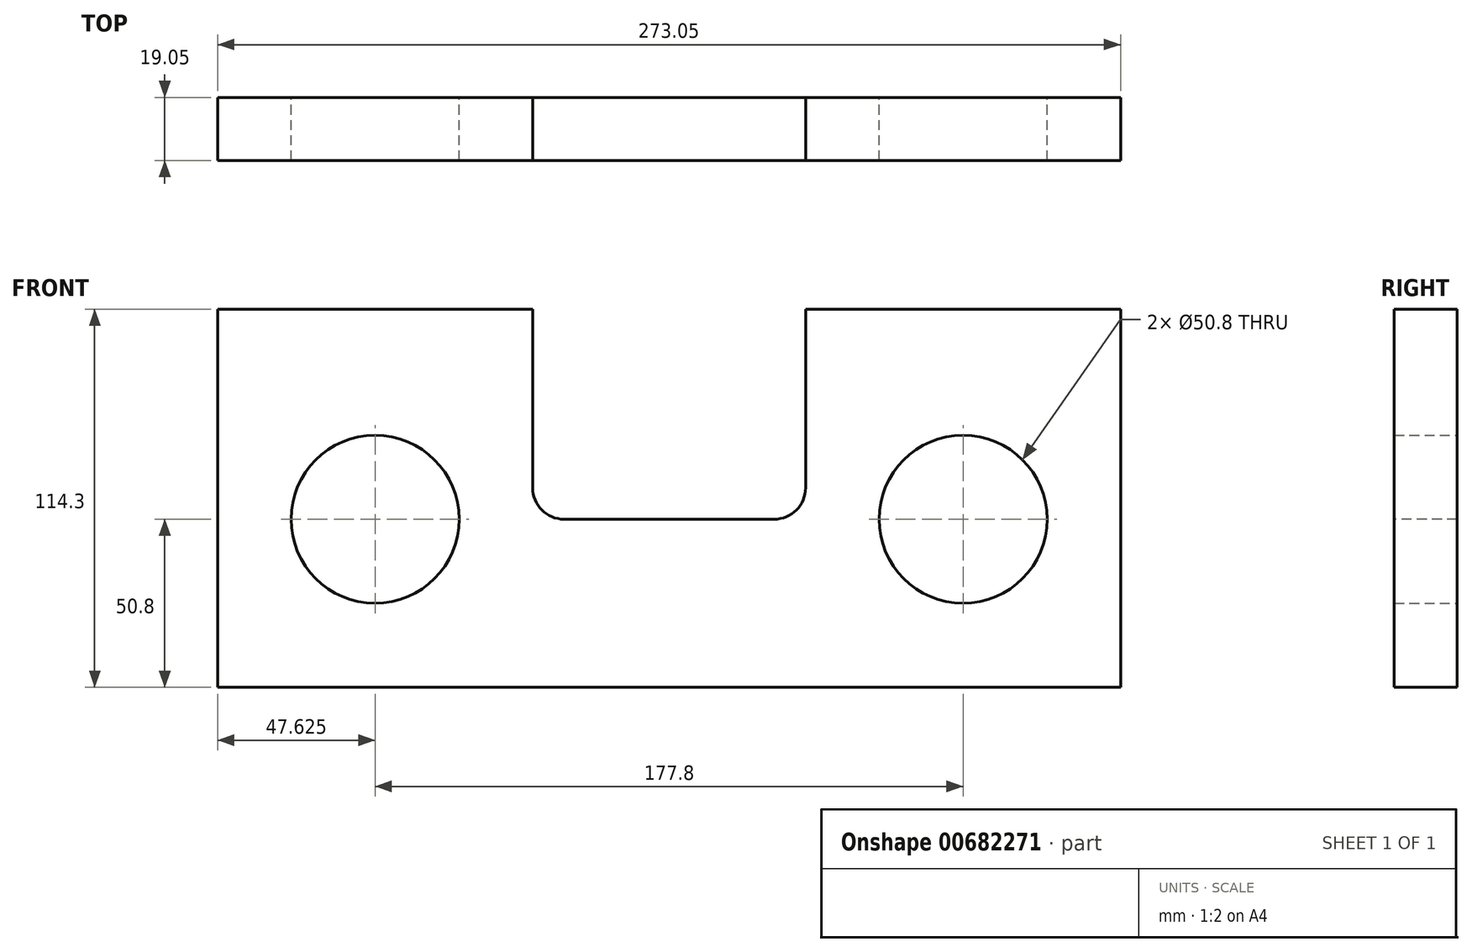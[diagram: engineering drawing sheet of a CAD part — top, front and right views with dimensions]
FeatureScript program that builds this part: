
annotation { "Feature Type Name" : "Feature", "Feature Type Description" : "" }
export const myFeature = defineFeature(function(context is Context, id is Id, definition is map)
    precondition{}
    {
        {
            var Q0;
            Q0=qCreatedBy(makeId("Front.planeOp"),FACE);
            var sketch = newSketch(context, id + "F0", { "sketchPlane" : qUnion([Q0])});
            skLineSegment(sketch, "E0.bottom", {"start": v(0, 0) * mm, "end": v(273.05, 0) * mm});
            skLineSegment(sketch, "E0.top", {"start": v(0, 114.3) * mm, "end": v(273.05, 114.3) * mm});
            skLineSegment(sketch, "E0.left", {"start": v(0, 0) * mm, "end": v(0, 114.3) * mm});
            skLineSegment(sketch, "E0.right", {"start": v(273.05, 0) * mm, "end": v(273.05, 114.3) * mm});
            skSolve(sketch);
        }
        {
            var Q0;
            Q0=makeQuery(id+"F0.imprint","IMPRINT",FACE,{"disambiguationData":[TD([[makeQuery(id+"F0.imprint","IMPRINT",EDGE,{"derivedFrom":sQuery(id+"F0.wireOp",EDGE,"E0.bottom")}),1.0]])]});
            var sketch = newSketch(context, id + "F1", { "sketchPlane" : qUnion([Q0])});
            skCircle(sketch, "E1", {"center": v(47.63, 50.8) * mm, "radius": 25.4 * mm});
            skCircle(sketch, "E2", {"center": v(225.43, 50.8) * mm, "radius": 25.4 * mm});
            skSolve(sketch);
        }
        {
            var Q0;
            Q0=makeQuery(id+"F1.imprint","IMPRINT",FACE,{"disambiguationData":[TD([[makeQuery(id+"F1.imprint","IMPRINT",EDGE,{"derivedFrom":sQuery(id+"F1.wireOp",EDGE,"E1")}),-1.0]])]});
            extrude(context, id + "F2", {"entities" : qUnion([Q0]), "depth" : 19.05 * mm, "offsetDistance" : 25.4 * mm});
        }
        {
            var Q0;
            Q0=qSketchRegion(id+"F1",true);
            extrude(context, id + "F3", {"entities" : qUnion([Q0]), "operationType" : NewBodyOperationType.REMOVE, "oppositeDirection" : true, "depth" : 25.4 * mm, "offsetDistance" : 25.4 * mm});
        }
        {
            var Q0;
            Q0=makeQuery(id+"F2.opExtrude","CAP_FACE",FACE,{"disambiguationData":[OSD([sQuery(id+"F0.wireOp",EDGE,"E0.bottom"),sQuery(id+"F0.wireOp",EDGE,"E0.top"),sQuery(id+"F0.wireOp",EDGE,"E0.left"),sQuery(id+"F0.wireOp",EDGE,"E0.right"),sQuery(id+"F1.wireOp",EDGE,"E1"),sQuery(id+"F1.wireOp",EDGE,"E2")])],"isStart":false});
            var sketch = newSketch(context, id + "F4", { "sketchPlane" : qUnion([Q0])});
            skLineSegment(sketch, "E3", {"start": v(95.25, 114.3) * mm, "end": v(95.25, 60.32) * mm});
            skLineSegment(sketch, "E4", {"start": v(104.78, 50.8) * mm, "end": v(168.28, 50.8) * mm});
            skLineSegment(sketch, "E5", {"start": v(177.8, 60.33) * mm, "end": v(177.8, 114.3) * mm});
            skLineSegment(sketch, "E6", {"start": v(95.25, 114.3) * mm, "end": v(177.8, 114.3) * mm});
            skPoint(sketch, "E7.visualSharp", {"position": v(95.25, 50.8) * mm});
            skArc(sketch, "E7.filletArc", {"start": v(95.25, 60.32) * mm, "mid": v(98.04, 53.59) * mm, "end": v(104.78, 50.8) * mm});
            skPoint(sketch, "E8.visualSharp", {"position": v(177.8, 50.8) * mm});
            skArc(sketch, "E8.filletArc", {"start": v(168.28, 50.8) * mm, "mid": v(175.01, 53.59) * mm, "end": v(177.8, 60.33) * mm});
            skSolve(sketch);
        }
        {
            var Q0;
            Q0 = qSketchRegion(id + "F4", true);
            extrude(context, id + "F5", {"entities" : qUnion([Q0]), "operationType" : NewBodyOperationType.REMOVE, "oppositeDirection" : true, "depth" : 25.4 * mm, "offsetDistance" : 25.4 * mm});
        }
    });
